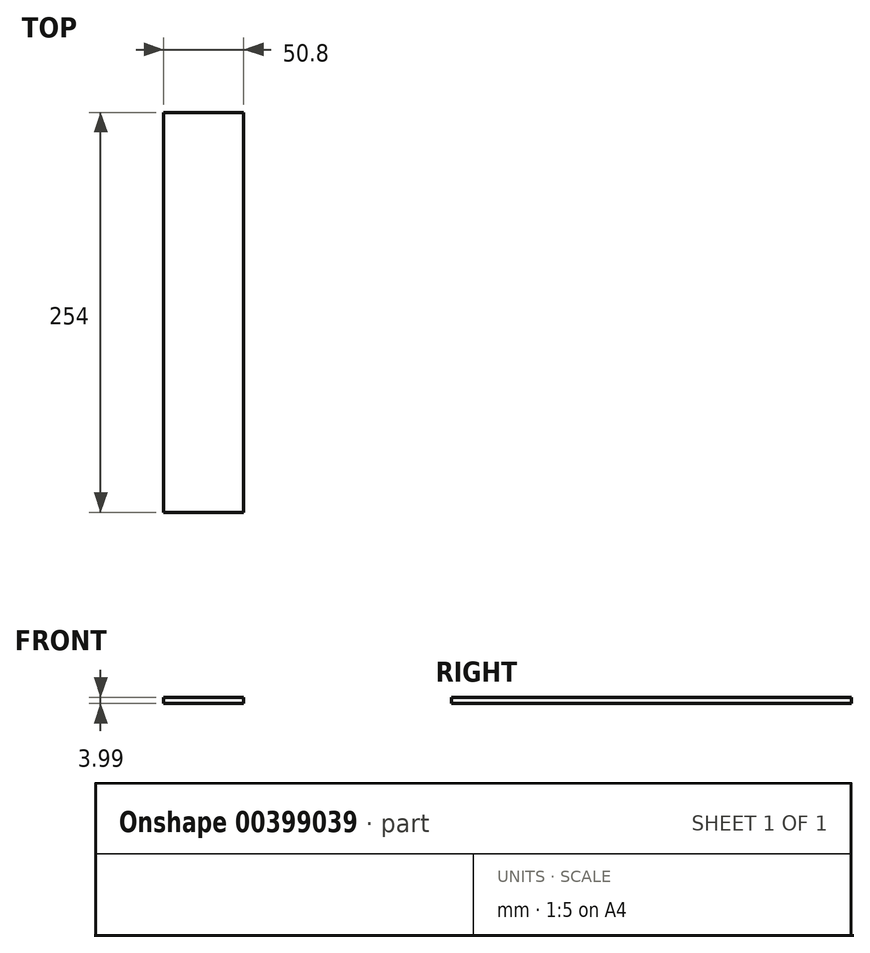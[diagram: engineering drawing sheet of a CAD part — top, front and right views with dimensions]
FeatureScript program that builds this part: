
annotation { "Feature Type Name" : "Feature", "Feature Type Description" : "" }
export const myFeature = defineFeature(function(context is Context, id is Id, definition is map)
    precondition{}
    {
        {
            var Q0;
            Q0=qCreatedBy(makeId("Top.planeOp"),FACE);
            var sketch = newSketch(context, id + "F0", { "sketchPlane" : qUnion([Q0])});
            skLineSegment(sketch, "E0.bottom", {"start": v(25.4, -127) * mm, "end": v(-25.4, -127) * mm});
            skLineSegment(sketch, "E0.top", {"start": v(25.4, 127) * mm, "end": v(-25.4, 127) * mm});
            skLineSegment(sketch, "E0.left", {"start": v(25.4, -127) * mm, "end": v(25.4, 127) * mm});
            skLineSegment(sketch, "E0.right", {"start": v(-25.4, -127) * mm, "end": v(-25.4, 127) * mm});
            skPoint(sketch, "E0.middle", {"position": v(0, 0) * mm});
            skSolve(sketch);
        }
        {
            var Q0;
            Q0=qSketchRegion(id+"F0",true);
            extrude(context, id + "F1", {"entities" : qUnion([Q0]), "depth" : 4 * mm});
        }
    });
